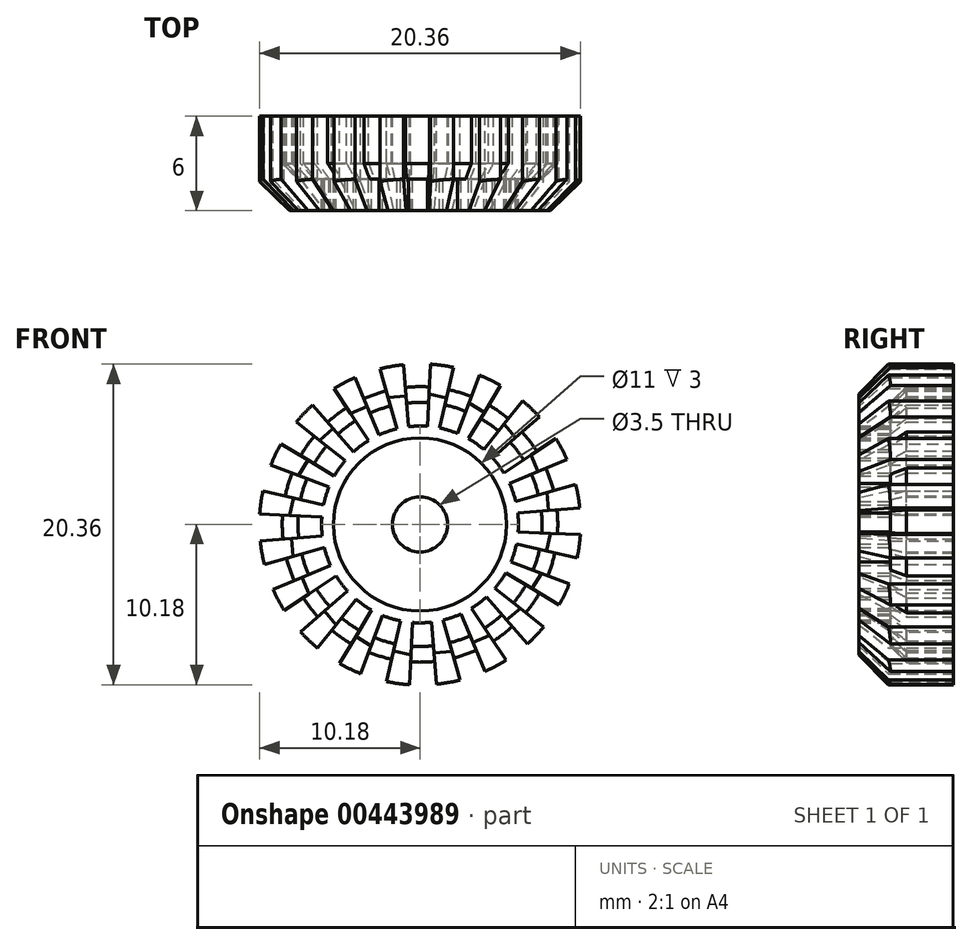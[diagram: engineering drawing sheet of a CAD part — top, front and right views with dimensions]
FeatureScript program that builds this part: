
annotation { "Feature Type Name" : "Feature", "Feature Type Description" : "" }
export const myFeature = defineFeature(function(context is Context, id is Id, definition is map)
    precondition{}
    {
        {
            var Q0;
            Q0=qCreatedBy(makeId("Front.planeOp"),FACE);
            var sketch = newSketch(context, id + "F0", { "sketchPlane" : qUnion([Q0])});
            skCircle(sketch, "E0", {"center": v(0, 0) * mm, "radius": 10.2 * mm});
            skCircle(sketch, "E1", {"center": v(0, 0) * mm, "radius": 1.75 * mm});
            skLineSegment(sketch, "E2", {"start": v(0, 0) * mm, "end": v(-0.2, 10.2) * mm});
            skLineSegment(sketch, "E3", {"start": v(0, 0) * mm, "end": v(-3.34, 9.64) * mm});
            skCircle(sketch, "E4", {"center": v(0, 0) * mm, "radius": 6.25 * mm});
            skCircle(sketch, "E5", {"center": v(0, 0) * mm, "radius": 8.75 * mm});
            skCircle(sketch, "E6", {"center": v(0, 0) * mm, "radius": 5.5 * mm});
            skLineSegment(sketch, "E7", {"start": v(-3.34, 9.64) * mm, "end": v(-0.2, 10.2) * mm, "construction": true});
            skLineSegment(sketch, "E8", {"start": v(-1.47, 6.07) * mm, "end": v(-2.53, 9.88) * mm});
            skLineSegment(sketch, "E9", {"start": v(-1.05, 10.15) * mm, "end": v(-0.72, 6.2) * mm});
            skSolve(sketch);
        }
        {
            var Q0;
            {var subQ3=sQuery(id+"F0.wireOp",EDGE,"E2");var subQ5=sQuery(id+"F0.wireOp",EDGE,"E6");var subQ9=makeQuery(id+"F0.imprint","INTERSECT",VERTEX,{"derivedFrom":[subQ3,subQ5]});Q0=makeQuery(id+"F0.imprint","IMPRINT",FACE,{"disambiguationData":[TD([[makeQuery(id+"F0.imprint","IMPRINT",EDGE,{"disambiguationData":[TD([[subQ9,-1.0]])],"derivedFrom":subQ3}),1.0]])]});}
            var Q1;
            {var subQ0=sQuery(id+"F0.wireOp",EDGE,"E8");var subQ1=sQuery(id+"F0.wireOp",EDGE,"E4");var subQ2=makeQuery(id+"F0.imprint","INTERSECT",VERTEX,{"derivedFrom":[subQ1,subQ0]});Q1=makeQuery(id+"F0.imprint","IMPRINT",FACE,{"disambiguationData":[TD([[makeQuery(id+"F0.imprint","IMPRINT",EDGE,{"disambiguationData":[TD([[subQ2,1.0]])],"derivedFrom":subQ1}),-1.0]])]});}
            var Q2;
            {var subQ0=sQuery(id+"F0.wireOp",EDGE,"E8");var subQ1=sQuery(id+"F0.wireOp",EDGE,"E0");var subQ2=makeQuery(id+"F0.imprint","INTERSECT",VERTEX,{"derivedFrom":[subQ1,subQ0]});Q2=makeQuery(id+"F0.imprint","IMPRINT",FACE,{"disambiguationData":[TD([[makeQuery(id+"F0.imprint","IMPRINT",EDGE,{"disambiguationData":[TD([[subQ2,1.0]])],"derivedFrom":subQ1}),1.0]])]});}
            extrude(context, id + "F1", {"entities" : qUnion([Q0, Q1, Q2]), "depth" : 6 * mm});
        }
        {
            var Q0;
            Q0=makeQuery(id+"F1.opExtrude","SWEPT_FACE",FACE,{"disambiguationData":[OSD([sQuery(id+"F0.wireOp",EDGE,"E9")])]});
            var sketch = newSketch(context, id + "F2", { "sketchPlane" : qUnion([Q0])});
            skLineSegment(sketch, "E10.0", {"start": v(-6, 6.25) * mm, "end": v(0, 6.25) * mm});
            skLineSegment(sketch, "E10.1", {"start": v(-6, 10.2) * mm, "end": v(-6, 6.25) * mm});
            skLineSegment(sketch, "E10.2", {"start": v(-6, 10.2) * mm, "end": v(0, 10.2) * mm});
            skLineSegment(sketch, "E10.3", {"start": v(0, 10.2) * mm, "end": v(0, 6.25) * mm});
            skLineSegment(sketch, "E11", {"start": v(-6, 8.2) * mm, "end": v(0, 8.2) * mm, "construction": true});
            skLineSegment(sketch, "E12", {"start": v(-4, 6.25) * mm, "end": v(-4, 10.2) * mm, "construction": true});
            skLineSegment(sketch, "E13", {"start": v(-4, 10.2) * mm, "end": v(-6, 8.2) * mm});
            skSolve(sketch);
        }
        {
            var Q0;
            {var subQ3=sQuery(id+"F2.wireOp",EDGE,"E13");Q0=makeQuery(id+"F2.imprint","IMPRINT",FACE,{"disambiguationData":[TD([[makeQuery(id+"F2.imprint","IMPRINT",EDGE,{"derivedFrom":subQ3}),-1.0]])]});}
            extrude(context, id + "F3", {"entities" : qUnion([Q0]), "operationType" : NewBodyOperationType.REMOVE, "endBound" : BoundingType.THROUGH_ALL, "oppositeDirection" : true, "depth" : 25 * mm});
        }
        {
            var Q0;
            Q0=makeQuery(id+"F1.opExtrude","SWEPT_BODY",BODY,{"disambiguationData":[OSD([sQuery(id+"F0.wireOp",EDGE,"E0"),sQuery(id+"F0.wireOp",EDGE,"E2"),sQuery(id+"F0.wireOp",EDGE,"E3"),sQuery(id+"F0.wireOp",EDGE,"E4"),sQuery(id+"F0.wireOp",EDGE,"E6"),sQuery(id+"F0.wireOp",EDGE,"E8"),sQuery(id+"F0.wireOp",EDGE,"E9")])]});
            var Q1;
            Q1=sQuery(id+"F0.wireOp",EDGE,"E6");
            circularPattern(context, id + "F4", {"operationType" : NewBodyOperationType.ADD, "entities" : qUnion([Q0]), "axis" : qUnion([Q1]), "angle" : 360 * degree, "instanceCount" : 20, "equalSpace" : true});
        }
        {
            var Q0;
            {var subQ0=sQuery(id+"F0.wireOp",EDGE,"E2");var subQ1=sQuery(id+"F0.wireOp",EDGE,"E1");var subQ2=makeQuery(id+"F0.imprint","INTERSECT",VERTEX,{"derivedFrom":[subQ1,subQ0]});Q0=makeQuery(id+"F0.imprint","IMPRINT",FACE,{"disambiguationData":[TD([[makeQuery(id+"F0.imprint","IMPRINT",EDGE,{"disambiguationData":[TD([[subQ2,1.0]])],"derivedFrom":subQ1}),-1.0]])]});}
            var Q1;
            {var subQ0=sQuery(id+"F0.wireOp",EDGE,"E2");var subQ1=sQuery(id+"F0.wireOp",EDGE,"E1");var subQ2=makeQuery(id+"F0.imprint","INTERSECT",VERTEX,{"derivedFrom":[subQ1,subQ0]});Q1=makeQuery(id+"F0.imprint","IMPRINT",FACE,{"disambiguationData":[TD([[makeQuery(id+"F0.imprint","IMPRINT",EDGE,{"disambiguationData":[TD([[subQ2,-1.0]])],"derivedFrom":subQ1}),-1.0]])]});}
            extrude(context, id + "F5", {"entities" : qUnion([Q0, Q1]), "operationType" : NewBodyOperationType.ADD, "depth" : 3 * mm});
        }
        {
            var Q0;
            {var subQ0=sQuery(id+"F0.wireOp",EDGE,"E4");var subQ1=sQuery(id+"F0.wireOp",EDGE,"E2");var subQ2=makeQuery(id+"F0.imprint","INTERSECT",VERTEX,{"derivedFrom":[subQ1,subQ0]});Q0=makeQuery(id+"F0.imprint","IMPRINT",FACE,{"disambiguationData":[TD([[makeQuery(id+"F0.imprint","IMPRINT",EDGE,{"disambiguationData":[TD([[subQ2,-1.0]])],"derivedFrom":subQ1}),-1.0]])]});}
            var Q1;
            {var subQ0=sQuery(id+"F0.wireOp",EDGE,"E4");var subQ1=sQuery(id+"F0.wireOp",EDGE,"E3");var subQ2=makeQuery(id+"F0.imprint","INTERSECT",VERTEX,{"derivedFrom":[subQ1,subQ0]});Q1=makeQuery(id+"F0.imprint","IMPRINT",FACE,{"disambiguationData":[TD([[makeQuery(id+"F0.imprint","IMPRINT",EDGE,{"disambiguationData":[TD([[subQ2,-1.0]])],"derivedFrom":subQ1}),-1.0]])]});}
            var Q2;
            {var subQ0=sQuery(id+"F0.wireOp",EDGE,"E4");var subQ1=sQuery(id+"F0.wireOp",EDGE,"E2");var subQ2=makeQuery(id+"F0.imprint","INTERSECT",VERTEX,{"derivedFrom":[subQ1,subQ0]});Q2=makeQuery(id+"F0.imprint","IMPRINT",FACE,{"disambiguationData":[TD([[makeQuery(id+"F0.imprint","IMPRINT",EDGE,{"disambiguationData":[TD([[subQ2,-1.0]])],"derivedFrom":subQ1}),1.0]])]});}
            extrude(context, id + "F6", {"entities" : qUnion([Q0, Q1, Q2]), "operationType" : NewBodyOperationType.ADD, "depth" : 4 * mm});
        }
        {
            var Q0;
            {var subQ0=sQuery(id+"F0.wireOp",EDGE,"E8");var subQ2=sQuery(id+"F0.wireOp",EDGE,"E5");Q0=makeQuery(id+"F6.boolean.opBoolean","SPLIT",EDGE,{"disambiguationData":[TD([makeQuery(id+"F4.opPattern","COPY",FACE,{"derivedFrom":makeQuery(id+"F1.opExtrude","SWEPT_FACE",FACE,{"disambiguationData":[OSD([subQ0])]}),"instanceName":"2"})])],"derivedFrom":makeQuery(id+"F6.opExtrude","CAP_EDGE",EDGE,{"disambiguationData":[OSD([subQ2])],"isStart":false})});}
            var Q1;
            {var subQ0=sQuery(id+"F0.wireOp",EDGE,"E8");var subQ2=sQuery(id+"F0.wireOp",EDGE,"E5");Q1=makeQuery(id+"F6.boolean.opBoolean","SPLIT",EDGE,{"disambiguationData":[TD([makeQuery(id+"F4.opPattern","COPY",FACE,{"derivedFrom":makeQuery(id+"F1.opExtrude","SWEPT_FACE",FACE,{"disambiguationData":[OSD([subQ0])]}),"instanceName":"1"})])],"derivedFrom":makeQuery(id+"F6.opExtrude","CAP_EDGE",EDGE,{"disambiguationData":[OSD([subQ2])],"isStart":false})});}
            var Q2;
            {var subQ0=sQuery(id+"F0.wireOp",EDGE,"E8");var subQ2=sQuery(id+"F0.wireOp",EDGE,"E5");Q2=makeQuery(id+"F6.boolean.opBoolean","SPLIT",EDGE,{"disambiguationData":[TD([makeQuery(id+"F1.opExtrude","SWEPT_FACE",FACE,{"disambiguationData":[OSD([subQ0])]})])],"derivedFrom":makeQuery(id+"F6.opExtrude","CAP_EDGE",EDGE,{"disambiguationData":[OSD([subQ2])],"isStart":false})});}
            var Q3;
            {var subQ0=sQuery(id+"F0.wireOp",EDGE,"E9");var subQ2=sQuery(id+"F0.wireOp",EDGE,"E5");Q3=makeQuery(id+"F6.boolean.opBoolean","SPLIT",EDGE,{"disambiguationData":[TD([makeQuery(id+"F1.opExtrude","SWEPT_FACE",FACE,{"disambiguationData":[OSD([subQ0])]})])],"derivedFrom":makeQuery(id+"F6.opExtrude","CAP_EDGE",EDGE,{"disambiguationData":[OSD([subQ2])],"isStart":false})});}
            var Q4;
            {var subQ0=sQuery(id+"F0.wireOp",EDGE,"E8");var subQ2=sQuery(id+"F0.wireOp",EDGE,"E5");Q4=makeQuery(id+"F6.boolean.opBoolean","SPLIT",EDGE,{"disambiguationData":[TD([makeQuery(id+"F4.opPattern","COPY",FACE,{"derivedFrom":makeQuery(id+"F1.opExtrude","SWEPT_FACE",FACE,{"disambiguationData":[OSD([subQ0])]}),"instanceName":"18"})])],"derivedFrom":makeQuery(id+"F6.opExtrude","CAP_EDGE",EDGE,{"disambiguationData":[OSD([subQ2])],"isStart":false})});}
            var Q5;
            {var subQ0=sQuery(id+"F0.wireOp",EDGE,"E8");var subQ2=sQuery(id+"F0.wireOp",EDGE,"E5");Q5=makeQuery(id+"F6.boolean.opBoolean","SPLIT",EDGE,{"disambiguationData":[TD([makeQuery(id+"F4.opPattern","COPY",FACE,{"derivedFrom":makeQuery(id+"F1.opExtrude","SWEPT_FACE",FACE,{"disambiguationData":[OSD([subQ0])]}),"instanceName":"17"})])],"derivedFrom":makeQuery(id+"F6.opExtrude","CAP_EDGE",EDGE,{"disambiguationData":[OSD([subQ2])],"isStart":false})});}
            var Q6;
            {var subQ0=sQuery(id+"F0.wireOp",EDGE,"E8");var subQ2=sQuery(id+"F0.wireOp",EDGE,"E5");Q6=makeQuery(id+"F6.boolean.opBoolean","SPLIT",EDGE,{"disambiguationData":[TD([makeQuery(id+"F4.opPattern","COPY",FACE,{"derivedFrom":makeQuery(id+"F1.opExtrude","SWEPT_FACE",FACE,{"disambiguationData":[OSD([subQ0])]}),"instanceName":"16"})])],"derivedFrom":makeQuery(id+"F6.opExtrude","CAP_EDGE",EDGE,{"disambiguationData":[OSD([subQ2])],"isStart":false})});}
            var Q7;
            {var subQ0=sQuery(id+"F0.wireOp",EDGE,"E8");var subQ2=sQuery(id+"F0.wireOp",EDGE,"E5");Q7=makeQuery(id+"F6.boolean.opBoolean","SPLIT",EDGE,{"disambiguationData":[TD([makeQuery(id+"F4.opPattern","COPY",FACE,{"derivedFrom":makeQuery(id+"F1.opExtrude","SWEPT_FACE",FACE,{"disambiguationData":[OSD([subQ0])]}),"instanceName":"15"})])],"derivedFrom":makeQuery(id+"F6.opExtrude","CAP_EDGE",EDGE,{"disambiguationData":[OSD([subQ2])],"isStart":false})});}
            var Q8;
            {var subQ0=sQuery(id+"F0.wireOp",EDGE,"E8");var subQ1=sQuery(id+"F0.wireOp",EDGE,"E5");Q8=makeQuery(id+"F6.boolean.opBoolean","SPLIT",EDGE,{"disambiguationData":[TD([makeQuery(id+"F4.opPattern","COPY",FACE,{"derivedFrom":makeQuery(id+"F1.opExtrude","SWEPT_FACE",FACE,{"disambiguationData":[OSD([subQ0])]}),"instanceName":"14"})])],"derivedFrom":makeQuery(id+"F6.opExtrude","CAP_EDGE",EDGE,{"disambiguationData":[OSD([subQ1])],"isStart":false})});}
            var Q9;
            {var subQ0=sQuery(id+"F0.wireOp",EDGE,"E8");var subQ2=sQuery(id+"F0.wireOp",EDGE,"E5");Q9=makeQuery(id+"F6.boolean.opBoolean","SPLIT",EDGE,{"disambiguationData":[TD([makeQuery(id+"F4.opPattern","COPY",FACE,{"derivedFrom":makeQuery(id+"F1.opExtrude","SWEPT_FACE",FACE,{"disambiguationData":[OSD([subQ0])]}),"instanceName":"13"})])],"derivedFrom":makeQuery(id+"F6.opExtrude","CAP_EDGE",EDGE,{"disambiguationData":[OSD([subQ2])],"isStart":false})});}
            var Q10;
            {var subQ0=sQuery(id+"F0.wireOp",EDGE,"E8");var subQ2=sQuery(id+"F0.wireOp",EDGE,"E5");Q10=makeQuery(id+"F6.boolean.opBoolean","SPLIT",EDGE,{"disambiguationData":[TD([makeQuery(id+"F4.opPattern","COPY",FACE,{"derivedFrom":makeQuery(id+"F1.opExtrude","SWEPT_FACE",FACE,{"disambiguationData":[OSD([subQ0])]}),"instanceName":"12"})])],"derivedFrom":makeQuery(id+"F6.opExtrude","CAP_EDGE",EDGE,{"disambiguationData":[OSD([subQ2])],"isStart":false})});}
            var Q11;
            {var subQ0=sQuery(id+"F0.wireOp",EDGE,"E8");var subQ2=sQuery(id+"F0.wireOp",EDGE,"E5");Q11=makeQuery(id+"F6.boolean.opBoolean","SPLIT",EDGE,{"disambiguationData":[TD([makeQuery(id+"F4.opPattern","COPY",FACE,{"derivedFrom":makeQuery(id+"F1.opExtrude","SWEPT_FACE",FACE,{"disambiguationData":[OSD([subQ0])]}),"instanceName":"11"})])],"derivedFrom":makeQuery(id+"F6.opExtrude","CAP_EDGE",EDGE,{"disambiguationData":[OSD([subQ2])],"isStart":false})});}
            var Q12;
            {var subQ0=sQuery(id+"F0.wireOp",EDGE,"E8");var subQ2=sQuery(id+"F0.wireOp",EDGE,"E5");Q12=makeQuery(id+"F6.boolean.opBoolean","SPLIT",EDGE,{"disambiguationData":[TD([makeQuery(id+"F4.opPattern","COPY",FACE,{"derivedFrom":makeQuery(id+"F1.opExtrude","SWEPT_FACE",FACE,{"disambiguationData":[OSD([subQ0])]}),"instanceName":"10"})])],"derivedFrom":makeQuery(id+"F6.opExtrude","CAP_EDGE",EDGE,{"disambiguationData":[OSD([subQ2])],"isStart":false})});}
            var Q13;
            {var subQ0=sQuery(id+"F0.wireOp",EDGE,"E8");var subQ2=sQuery(id+"F0.wireOp",EDGE,"E5");Q13=makeQuery(id+"F6.boolean.opBoolean","SPLIT",EDGE,{"disambiguationData":[TD([makeQuery(id+"F4.opPattern","COPY",FACE,{"derivedFrom":makeQuery(id+"F1.opExtrude","SWEPT_FACE",FACE,{"disambiguationData":[OSD([subQ0])]}),"instanceName":"3"})])],"derivedFrom":makeQuery(id+"F6.opExtrude","CAP_EDGE",EDGE,{"disambiguationData":[OSD([subQ2])],"isStart":false})});}
            var Q14;
            {var subQ0=sQuery(id+"F0.wireOp",EDGE,"E8");var subQ1=sQuery(id+"F0.wireOp",EDGE,"E5");Q14=makeQuery(id+"F6.boolean.opBoolean","SPLIT",EDGE,{"disambiguationData":[TD([makeQuery(id+"F4.opPattern","COPY",FACE,{"derivedFrom":makeQuery(id+"F1.opExtrude","SWEPT_FACE",FACE,{"disambiguationData":[OSD([subQ0])]}),"instanceName":"4"})])],"derivedFrom":makeQuery(id+"F6.opExtrude","CAP_EDGE",EDGE,{"disambiguationData":[OSD([subQ1])],"isStart":false})});}
            var Q15;
            {var subQ0=sQuery(id+"F0.wireOp",EDGE,"E8");var subQ2=sQuery(id+"F0.wireOp",EDGE,"E5");Q15=makeQuery(id+"F6.boolean.opBoolean","SPLIT",EDGE,{"disambiguationData":[TD([makeQuery(id+"F4.opPattern","COPY",FACE,{"derivedFrom":makeQuery(id+"F1.opExtrude","SWEPT_FACE",FACE,{"disambiguationData":[OSD([subQ0])]}),"instanceName":"5"})])],"derivedFrom":makeQuery(id+"F6.opExtrude","CAP_EDGE",EDGE,{"disambiguationData":[OSD([subQ2])],"isStart":false})});}
            var Q16;
            {var subQ0=sQuery(id+"F0.wireOp",EDGE,"E8");var subQ2=sQuery(id+"F0.wireOp",EDGE,"E5");Q16=makeQuery(id+"F6.boolean.opBoolean","SPLIT",EDGE,{"disambiguationData":[TD([makeQuery(id+"F4.opPattern","COPY",FACE,{"derivedFrom":makeQuery(id+"F1.opExtrude","SWEPT_FACE",FACE,{"disambiguationData":[OSD([subQ0])]}),"instanceName":"6"})])],"derivedFrom":makeQuery(id+"F6.opExtrude","CAP_EDGE",EDGE,{"disambiguationData":[OSD([subQ2])],"isStart":false})});}
            var Q17;
            {var subQ0=sQuery(id+"F0.wireOp",EDGE,"E8");var subQ2=sQuery(id+"F0.wireOp",EDGE,"E5");Q17=makeQuery(id+"F6.boolean.opBoolean","SPLIT",EDGE,{"disambiguationData":[TD([makeQuery(id+"F4.opPattern","COPY",FACE,{"derivedFrom":makeQuery(id+"F1.opExtrude","SWEPT_FACE",FACE,{"disambiguationData":[OSD([subQ0])]}),"instanceName":"7"})])],"derivedFrom":makeQuery(id+"F6.opExtrude","CAP_EDGE",EDGE,{"disambiguationData":[OSD([subQ2])],"isStart":false})});}
            var Q18;
            {var subQ0=sQuery(id+"F0.wireOp",EDGE,"E8");var subQ2=sQuery(id+"F0.wireOp",EDGE,"E5");Q18=makeQuery(id+"F6.boolean.opBoolean","SPLIT",EDGE,{"disambiguationData":[TD([makeQuery(id+"F4.opPattern","COPY",FACE,{"derivedFrom":makeQuery(id+"F1.opExtrude","SWEPT_FACE",FACE,{"disambiguationData":[OSD([subQ0])]}),"instanceName":"8"})])],"derivedFrom":makeQuery(id+"F6.opExtrude","CAP_EDGE",EDGE,{"disambiguationData":[OSD([subQ2])],"isStart":false})});}
            var Q19;
            {var subQ0=sQuery(id+"F0.wireOp",EDGE,"E8");var subQ1=sQuery(id+"F0.wireOp",EDGE,"E5");Q19=makeQuery(id+"F6.boolean.opBoolean","SPLIT",EDGE,{"disambiguationData":[TD([makeQuery(id+"F4.opPattern","COPY",FACE,{"derivedFrom":makeQuery(id+"F1.opExtrude","SWEPT_FACE",FACE,{"disambiguationData":[OSD([subQ0])]}),"instanceName":"9"})])],"derivedFrom":makeQuery(id+"F6.opExtrude","CAP_EDGE",EDGE,{"disambiguationData":[OSD([subQ1])],"isStart":false})});}
            chamfer(context, id + "F7", {"entities" : qUnion([Q0, Q1, Q2, Q3, Q4, Q5, Q6, Q7, Q8, Q9, Q10, Q11, Q12, Q13, Q14, Q15, Q16, Q17, Q18, Q19]), "width" : 1 * mm, "tangentPropagation" : true});
        }
    });
